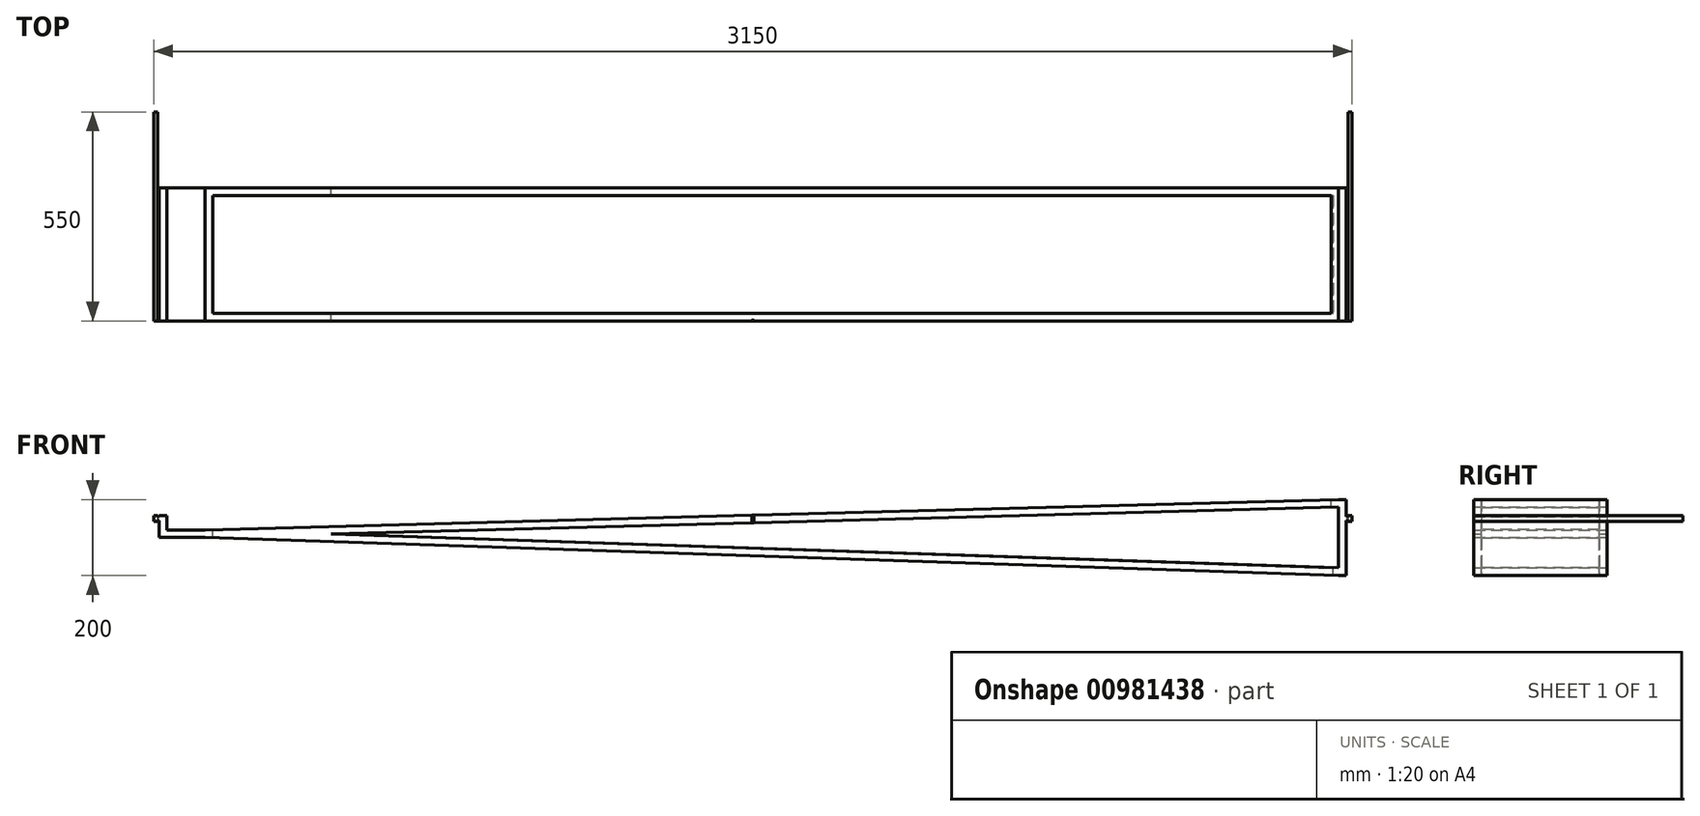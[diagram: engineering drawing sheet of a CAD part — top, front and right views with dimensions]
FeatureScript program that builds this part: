
annotation { "Feature Type Name" : "Feature", "Feature Type Description" : "" }
export const myFeature = defineFeature(function(context is Context, id is Id, definition is map)
    precondition{}
    {
        {
            var Q0;
            Q0=qCreatedBy(makeId("Front.planeOp"),FACE);
            var sketch = newSketch(context, id + "F0", { "sketchPlane" : qUnion([Q0])});
            skLineSegment(sketch, "E0", {"start": v(-10, 30) * mm, "end": v(-10, -130) * mm});
            skLineSegment(sketch, "E1", {"start": v(-10, -150) * mm, "end": v(10, -150) * mm});
            skLineSegment(sketch, "E2", {"start": v(10, -150) * mm, "end": v(10, -5) * mm});
            skLineSegment(sketch, "E3", {"start": v(10, 50) * mm, "end": v(-10, 50) * mm});
            skLineSegment(sketch, "E4", {"start": v(25, -7.5) * mm, "end": v(25, 7.5) * mm});
            skLineSegment(sketch, "E5", {"start": v(25, 7.5) * mm, "end": v(15, 7.5) * mm});
            skLineSegment(sketch, "E6", {"start": v(15, 7.5) * mm, "end": v(15, 5) * mm});
            skLineSegment(sketch, "E7", {"start": v(15, 5) * mm, "end": v(10, 5) * mm});
            skLineSegment(sketch, "E8", {"start": v(25, -7.5) * mm, "end": v(15, -7.5) * mm});
            skLineSegment(sketch, "E9", {"start": v(15, -7.5) * mm, "end": v(15, -5) * mm});
            skLineSegment(sketch, "E10", {"start": v(15, -5) * mm, "end": v(10, -5) * mm});
            skLineSegment(sketch, "E11.trimOffspring", {"start": v(10, 5) * mm, "end": v(10, 50) * mm});
            skLineSegment(sketch, "E12.MirrorCS", {"start": v(-3115, 7.5) * mm, "end": v(-3115, 5) * mm});
            skLineSegment(sketch, "E13.MirrorCS", {"start": v(-3115, -7.5) * mm, "end": v(-3115, -5) * mm});
            skLineSegment(sketch, "E14.MirrorCS", {"start": v(-3115, 5) * mm, "end": v(-3110, 5) * mm});
            skLineSegment(sketch, "E15.MirrorCS", {"start": v(-3115, -5) * mm, "end": v(-3110, -5) * mm});
            skLineSegment(sketch, "E16.MirrorCS", {"start": v(-3125, -7.5) * mm, "end": v(-3115, -7.5) * mm});
            skLineSegment(sketch, "E17.MirrorCS", {"start": v(-3125, -7.5) * mm, "end": v(-3125, 7.5) * mm});
            skLineSegment(sketch, "E18.MirrorCS", {"start": v(-3125, 7.5) * mm, "end": v(-3115, 7.5) * mm});
            skLineSegment(sketch, "E19.MirrorCS", {"start": v(-3110, 5) * mm, "end": v(-3110, 7.5) * mm});
            skLineSegment(sketch, "E20.MirrorCS", {"start": v(-3090, 7.5) * mm, "end": v(-3090, -30) * mm});
            skLineSegment(sketch, "E21.MirrorCS", {"start": v(-3110, -50) * mm, "end": v(-3110, -5) * mm});
            skLineSegment(sketch, "E22", {"start": v(-3110, 7.5) * mm, "end": v(-3090, 7.5) * mm});
            skLineSegment(sketch, "E23", {"start": v(-3090, -30) * mm, "end": v(-2990, -30) * mm});
            skLineSegment(sketch, "E24", {"start": v(-2990, -50) * mm, "end": v(-3110, -50) * mm});
            skPoint(sketch, "E25", {"position": v(-10, -130) * mm});
            skPoint(sketch, "E26", {"position": v(-10, 30) * mm});
            skLineSegment(sketch, "E27", {"start": v(-10, -150) * mm, "end": v(-2990, -50) * mm});
            skLineSegment(sketch, "E28", {"start": v(-2658.89, -41.11) * mm, "end": v(-10, -130) * mm});
            skLineSegment(sketch, "E29", {"start": v(-10, 30) * mm, "end": v(-2658.89, -41.11) * mm});
            skLineSegment(sketch, "E30", {"start": v(-2990, -30) * mm, "end": v(-10, 50) * mm});
            skSolve(sketch);
        }
        {
            var Q0;
            Q0=makeQuery(id+"F0.imprint","IMPRINT",FACE,{"disambiguationData":[TD([[makeQuery(id+"F0.imprint","IMPRINT",EDGE,{"derivedFrom":sQuery(id+"F0.wireOp",EDGE,"E0")}),1.0]])]});
            extrude(context, id + "F1", {"entities" : qUnion([Q0]), "depth" : 350 * mm, "offsetDistance" : 25 * mm});
        }
        {
            var Q0;
            Q0=makeQuery(id+"F1.opExtrude","SWEPT_FACE",FACE,{"disambiguationData":[OSD([sQuery(id+"F0.wireOp",EDGE,"E30")])]});
            cPlane(context, id + "F2", {"entities" : qUnion([Q0]), "cplaneType" : CPlaneType.OFFSET, "offset" : 0 * mm, "width" : 150 * mm, "height" : 150 * mm});
        }
        {
            var Q0;
            Q0=qCreatedBy(id+"F2.planeOp",FACE);
            var sketch = newSketch(context, id + "F3", { "sketchPlane" : qUnion([Q0])});
            skLineSegment(sketch, "E31.bottom", {"start": v(-8.66, 0) * mm, "end": v(-2989.73, 0) * mm});
            skLineSegment(sketch, "E31.top", {"start": v(-8.66, -350) * mm, "end": v(-2989.73, -350) * mm});
            skLineSegment(sketch, "E31.left", {"start": v(-8.66, 0) * mm, "end": v(-8.66, -350) * mm});
            skLineSegment(sketch, "E31.right", {"start": v(-2989.73, 0) * mm, "end": v(-2989.73, -350) * mm});
            skLineSegment(sketch, "E32.0", {"start": v(-28.66, -20) * mm, "end": v(-2969.73, -20) * mm});
            skLineSegment(sketch, "E32.1", {"start": v(-28.66, -20) * mm, "end": v(-28.66, -330) * mm});
            skLineSegment(sketch, "E32.2", {"start": v(-28.66, -330) * mm, "end": v(-2969.73, -330) * mm});
            skLineSegment(sketch, "E32.3", {"start": v(-2969.73, -20) * mm, "end": v(-2969.73, -330) * mm});
            skSolve(sketch);
        }
        {
            var Q0;
            Q0=makeQuery(id+"F3.imprint","IMPRINT",FACE,{"disambiguationData":[TD([[makeQuery(id+"F3.imprint","IMPRINT",EDGE,{"derivedFrom":sQuery(id+"F3.wireOp",EDGE,"E32.0")}),1.0]])]});
            extrude(context, id + "F4", {"entities" : qUnion([Q0]), "operationType" : NewBodyOperationType.REMOVE, "oppositeDirection" : true, "depth" : 250 * mm, "offsetDistance" : 25 * mm});
        }
        {
            var Q0;
            Q0=makeQuery(id+"F1.opExtrude","CAP_FACE",FACE,{"disambiguationData":[OSD([sQuery(id+"F0.wireOp",EDGE,"E0"),sQuery(id+"F0.wireOp",EDGE,"E1"),sQuery(id+"F0.wireOp",EDGE,"E2"),sQuery(id+"F0.wireOp",EDGE,"E3"),sQuery(id+"F0.wireOp",EDGE,"E4"),sQuery(id+"F0.wireOp",EDGE,"E5"),sQuery(id+"F0.wireOp",EDGE,"E6"),sQuery(id+"F0.wireOp",EDGE,"E7"),sQuery(id+"F0.wireOp",EDGE,"E8"),sQuery(id+"F0.wireOp",EDGE,"E9"),sQuery(id+"F0.wireOp",EDGE,"E10"),sQuery(id+"F0.wireOp",EDGE,"E11.trimOffspring"),sQuery(id+"F0.wireOp",EDGE,"E12.MirrorCS"),sQuery(id+"F0.wireOp",EDGE,"E13.MirrorCS"),sQuery(id+"F0.wireOp",EDGE,"E14.MirrorCS"),sQuery(id+"F0.wireOp",EDGE,"E15.MirrorCS"),sQuery(id+"F0.wireOp",EDGE,"E16.MirrorCS"),sQuery(id+"F0.wireOp",EDGE,"E17.MirrorCS"),sQuery(id+"F0.wireOp",EDGE,"E18.MirrorCS"),sQuery(id+"F0.wireOp",EDGE,"E19.MirrorCS"),sQuery(id+"F0.wireOp",EDGE,"E20.MirrorCS"),sQuery(id+"F0.wireOp",EDGE,"E21.MirrorCS"),sQuery(id+"F0.wireOp",EDGE,"E22"),sQuery(id+"F0.wireOp",EDGE,"E23"),sQuery(id+"F0.wireOp",EDGE,"E24"),sQuery(id+"F0.wireOp",EDGE,"E27"),sQuery(id+"F0.wireOp",EDGE,"E28"),sQuery(id+"F0.wireOp",EDGE,"E29"),sQuery(id+"F0.wireOp",EDGE,"E30")])],"isStart":true});
            cPlane(context, id + "F5", {"entities" : qUnion([Q0]), "cplaneType" : CPlaneType.OFFSET, "offset" : 0 * mm, "width" : 150 * mm, "height" : 150 * mm});
        }
        {
            var Q0;
            Q0=qCreatedBy(id+"F5.planeOp",FACE);
            var sketch = newSketch(context, id + "F6", { "sketchPlane" : qUnion([Q0])});
            skLineSegment(sketch, "E33.bottom", {"start": v(-25, 7.5) * mm, "end": v(-15, 7.5) * mm});
            skLineSegment(sketch, "E33.top", {"start": v(-25, -7.5) * mm, "end": v(-15, -7.5) * mm});
            skLineSegment(sketch, "E33.left", {"start": v(-25, 7.5) * mm, "end": v(-25, -7.5) * mm});
            skLineSegment(sketch, "E33.right", {"start": v(-15, 7.5) * mm, "end": v(-15, -7.5) * mm});
            skLineSegment(sketch, "E34", {"start": v(3125, 7.5) * mm, "end": v(3125, -7.5) * mm});
            skLineSegment(sketch, "E35", {"start": v(3125, -7.5) * mm, "end": v(3115, -7.5) * mm});
            skLineSegment(sketch, "E36", {"start": v(3115, -7.5) * mm, "end": v(3115, 7.5) * mm});
            skLineSegment(sketch, "E37", {"start": v(3115, 7.5) * mm, "end": v(3125, 7.5) * mm});
            skSolve(sketch);
        }
        {
            var Q0;
            Q0 = qSketchRegion(id + "F6", true);
            extrude(context, id + "F7", {"entities" : qUnion([Q0]), "operationType" : NewBodyOperationType.ADD, "depth" : 200 * mm, "offsetDistance" : 25 * mm});
        }
        {
            var Q0;
            Q0=makeQuery(id+"F1.opExtrude","SWEPT_FACE",FACE,{"disambiguationData":[OSD([sQuery(id+"F0.wireOp",EDGE,"E30")])]});
            cPlane(context, id + "F8", {"entities" : qUnion([Q0]), "cplaneType" : CPlaneType.OFFSET, "offset" : 0 * mm, "width" : 150 * mm, "height" : 150 * mm});
        }
        {
            var Q0;
            Q0=qCreatedBy(id+"F8.planeOp",FACE);
            var sketch = newSketch(context, id + "F9", { "sketchPlane" : qUnion([Q0])});
            skPoint(sketch, "E38", {"position": v(-1549.2, -350) * mm});
            skSolve(sketch);
        }
        {
            var Q0;
            Q0=sQuery(id+"F9.wireOp",VERTEX,"E38");
            var Q1;
            Q1=makeQuery(id+"F1.opExtrude","SWEPT_BODY",BODY,{"disambiguationData":[OSD([sQuery(id+"F0.wireOp",EDGE,"E0"),sQuery(id+"F0.wireOp",EDGE,"E1"),sQuery(id+"F0.wireOp",EDGE,"E2"),sQuery(id+"F0.wireOp",EDGE,"E3"),sQuery(id+"F0.wireOp",EDGE,"E4"),sQuery(id+"F0.wireOp",EDGE,"E5"),sQuery(id+"F0.wireOp",EDGE,"E6"),sQuery(id+"F0.wireOp",EDGE,"E7"),sQuery(id+"F0.wireOp",EDGE,"E8"),sQuery(id+"F0.wireOp",EDGE,"E9"),sQuery(id+"F0.wireOp",EDGE,"E10"),sQuery(id+"F0.wireOp",EDGE,"E11.trimOffspring"),sQuery(id+"F0.wireOp",EDGE,"E12.MirrorCS"),sQuery(id+"F0.wireOp",EDGE,"E13.MirrorCS"),sQuery(id+"F0.wireOp",EDGE,"E14.MirrorCS"),sQuery(id+"F0.wireOp",EDGE,"E15.MirrorCS"),sQuery(id+"F0.wireOp",EDGE,"E16.MirrorCS"),sQuery(id+"F0.wireOp",EDGE,"E17.MirrorCS"),sQuery(id+"F0.wireOp",EDGE,"E18.MirrorCS"),sQuery(id+"F0.wireOp",EDGE,"E19.MirrorCS"),sQuery(id+"F0.wireOp",EDGE,"E20.MirrorCS"),sQuery(id+"F0.wireOp",EDGE,"E21.MirrorCS"),sQuery(id+"F0.wireOp",EDGE,"E22"),sQuery(id+"F0.wireOp",EDGE,"E23"),sQuery(id+"F0.wireOp",EDGE,"E24"),sQuery(id+"F0.wireOp",EDGE,"E27"),sQuery(id+"F0.wireOp",EDGE,"E28"),sQuery(id+"F0.wireOp",EDGE,"E29"),sQuery(id+"F0.wireOp",EDGE,"E30")])]});
            hole(context, id + "F10", {"style" : HoleStyle.SIMPLE, "endStyle" : HoleEndStyle.BLIND, "holeDiameter" : 5 * mm, "majorDiameter" : 5 * mm, "holeDepth" : 50 * mm, "isTappedThrough" : true, "tappedDepth" : 12 * mm, "tapClearance" : 3, "startFromSketch" : true, "locations" : qUnion([Q0]), "scope" : qUnion([Q1])});
        }
    });
